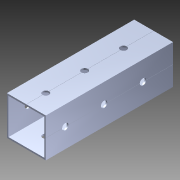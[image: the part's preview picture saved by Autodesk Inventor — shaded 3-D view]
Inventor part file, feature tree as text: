
AUTODESK INVENTOR PART (.ipt)
format: ipt  version: 2014 (Build 180170000, 170)  size: 1,121,280 bytes
history: native  units: in
note: dims shown in document units (in); Inventor stores cm internally (conversion verified against a paired STEP export)
features: pattern_circular x1, other x1, plane x1, extrude x1, imported_body x1, sketch x1
ambient origin geometry x8: Origin, YZ Plane, XZ Plane, XY Plane, X Axis, Y Axis, Z Axis, Center Point
bodies: Body1 (feature_tree)
feature tree (6):
  pattern_circular  "CirPattern2"
  other  "217-3426-STEP1"
  plane  "Work Plane1"
  extrude  "Extrusion1"  Depth=3937.0079in TaperAngle=0.0deg
  imported_body  "Base1"
  sketch  "Sketch1"  dims[d0=-3.275in d1=3937.0079in d2=0.0in]
